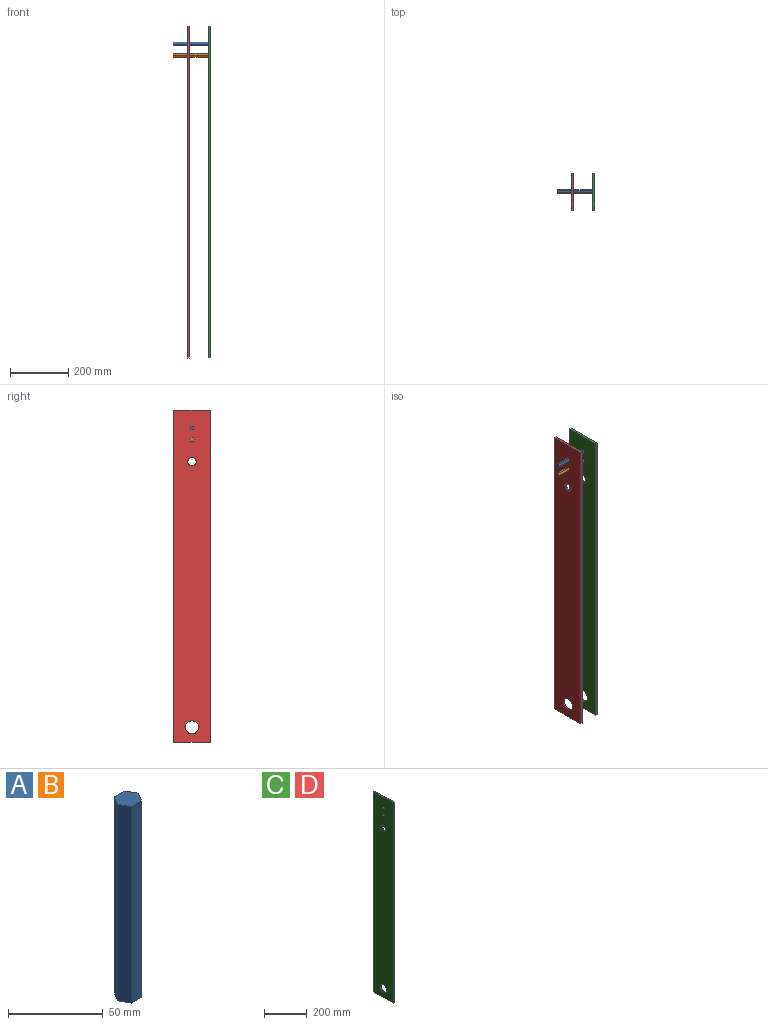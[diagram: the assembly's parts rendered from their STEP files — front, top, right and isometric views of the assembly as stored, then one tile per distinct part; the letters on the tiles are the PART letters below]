
ASSEMBLY  parts=4 mates=3
PART A: 8 faces, bbox 15x13x127 mm
  f0: plane 127x7.48mm, normal (0,1,0), area 949.8mm2, adj f1,f5,f6,f7
  f1: plane 127x6.48mm, normal (-0.87,0.5,0), area 949.8mm2, adj f0,f2,f6,f7
  f2: plane 127x6.48mm, normal (-0.87,-0.5,0), area 949.8mm2, adj f1,f3,f6,f7
  f3: plane 127x7.48mm, normal (0,-1,0), area 949.8mm2, adj f2,f4,f6,f7
  f4: plane 127x6.48mm, normal (0.87,-0.5,0), area 949.8mm2, adj f3,f5,f6,f7
  f5: plane 127x6.48mm, normal (0.87,0.5,0), area 949.8mm2, adj f0,f4,f6,f7
  f6: plane 14.96x12.95mm, normal (0,0,1), area 145.3mm2, adj f0,f1,f2,f3,f4,f5
  f7: plane 14.96x12.95mm, normal (0,0,-1), area 145.3mm2, adj f0,f1,f2,f3,f4,f5
PART B: same geometry as A
PART C: 20 faces, bbox 6.4x127x1143 mm
  f0: plane 1143x127mm, normal (1,0,0), area 142638mm2, adj f2,f3,f4,f5,f6,f7,f8,f9
  f1: plane 1143x127mm, normal (-1,0,0), area 142638mm2, adj f2,f3,f4,f5,f6,f7,f8,f9
  f2: plane 1143x6.35mm, normal (0,-1,0), area 7258mm2, adj f0,f1,f3,f5
  f3: plane 127x6.35mm, normal (0,0,-1), area 806.5mm2, adj f0,f1,f2,f4
  f4: plane 1143x6.35mm, normal (0,1,0), area 7258mm2, adj f0,f1,f3,f5
  f5: plane 127x6.35mm, normal (0,0,1), area 806.5mm2, adj f0,f1,f2,f4
  f6: cylinder r=14.29mm len=28.58mm, axis (1,0,0), area 570mm2, adj f0,f1
  f7: plane 7.48x6.35mm, normal (0,0,-1), area 47.5mm2, adj f0,f1,f8,f12
  f8: plane 6.48x6.35mm, normal (0,0.87,-0.5), area 47.5mm2, adj f0,f1,f7,f9
  f9: plane 6.48x6.35mm, normal (0,0.87,0.5), area 47.5mm2, adj f0,f1,f8,f10
  f10: plane 7.48x6.35mm, normal (0,0,1), area 47.5mm2, adj f0,f1,f9,f11
  f11: plane 6.48x6.35mm, normal (0,-0.87,0.5), area 47.5mm2, adj f0,f1,f10,f12
  f12: plane 6.48x6.35mm, normal (0,-0.87,-0.5), area 47.5mm2, adj f0,f1,f7,f11
  f13: plane 7.48x6.35mm, normal (0,0,1), area 47.5mm2, adj f0,f1,f14,f18
  f14: plane 6.48x6.35mm, normal (0,-0.87,0.5), area 47.5mm2, adj f0,f1,f13,f15
  f15: plane 6.48x6.35mm, normal (0,-0.87,-0.5), area 47.5mm2, adj f0,f1,f14,f16
  f16: plane 7.48x6.35mm, normal (0,0,-1), area 47.5mm2, adj f0,f1,f15,f17
  f17: plane 6.48x6.35mm, normal (0,0.87,-0.5), area 47.5mm2, adj f0,f1,f16,f18
  f18: plane 6.48x6.35mm, normal (0,0.87,0.5), area 47.5mm2, adj f0,f1,f13,f17
  f19: cylinder r=22.5mm len=45.01mm, axis (1,0,0), area 897.9mm2, adj f0,f1
PART D: same geometry as C
PLACE A rot(axis=(-0.58,0.58,-0.58),120deg) t=(-168.91,63.39,1049.08)mm
PLACE B rot(axis=(-0.25,0.94,-0.25),93.8deg) t=(-168.91,63.39,1010.98)mm
PLACE C t=(-47.63,-0.11,-31.69)mm
PLACE D t=(-121.29,-0.11,-31.69)mm
MATE fastened B.f0 <-> D.f11  axis (0,0.87,-0.5) through (-168.91,69,1007.75)mm
MATE fastened A.f1 <-> D.f14  axis (0,0.87,-0.5) through (-168.91,69,1045.85)mm
MATE fastened B.f2 <-> C.f7  axis (0,0,1) through (-41.91,63.39,1017.46)mm
